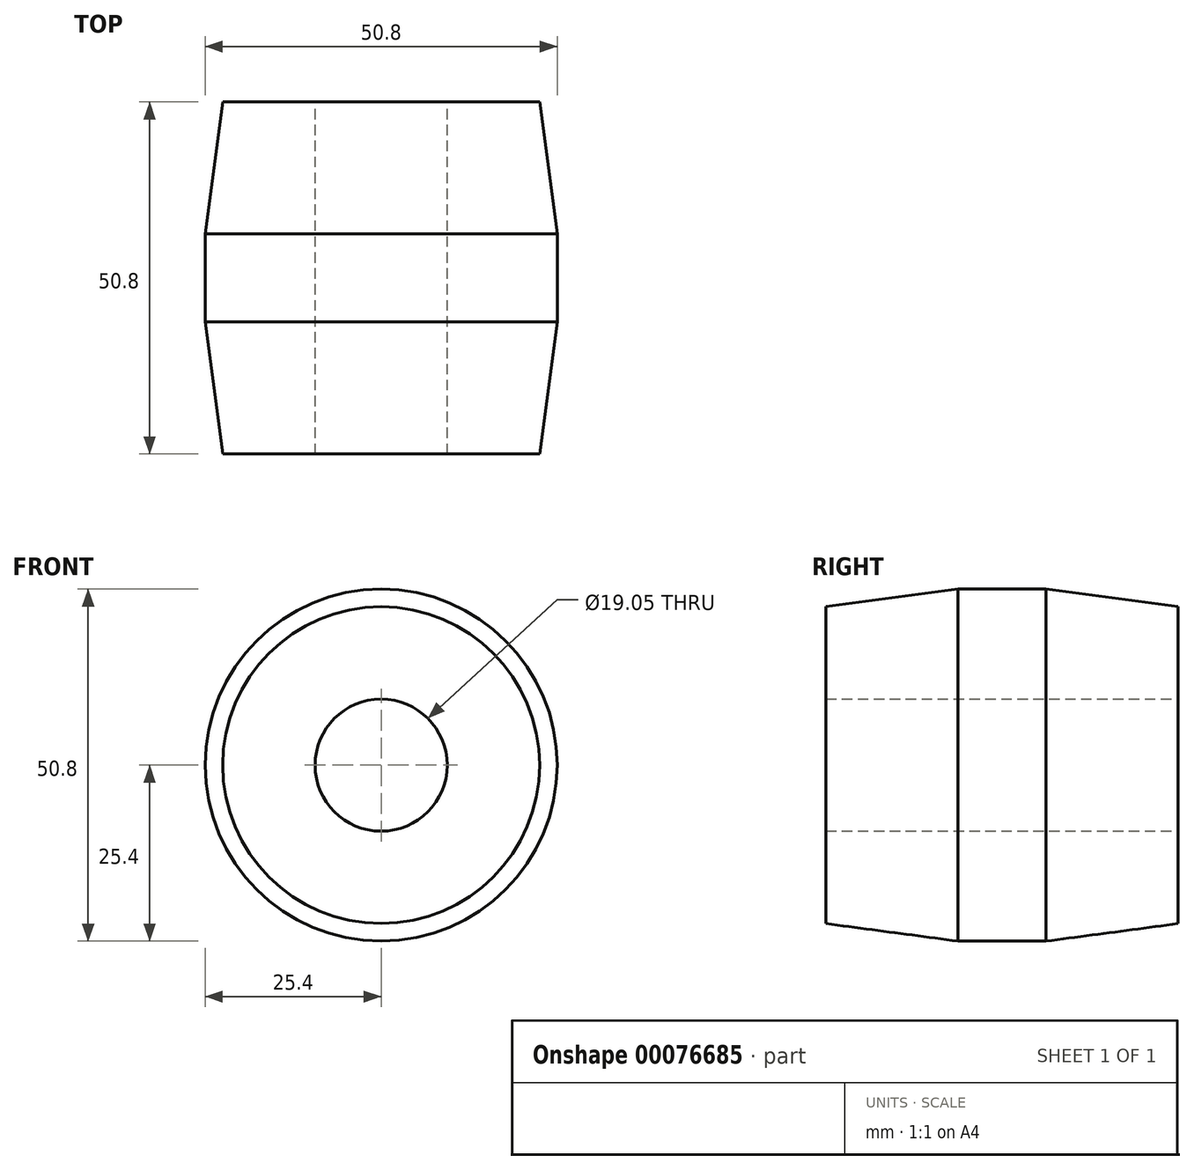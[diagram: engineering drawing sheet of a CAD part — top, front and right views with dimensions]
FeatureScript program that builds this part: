
annotation { "Feature Type Name" : "Feature", "Feature Type Description" : "" }
export const myFeature = defineFeature(function(context is Context, id is Id, definition is map)
    precondition{}
    {
        {
            var Q0;
            Q0=qCreatedBy(makeId("Front.planeOp"),FACE);
            var sketch = newSketch(context, id + "F0", { "sketchPlane" : qUnion([Q0])});
            skCircle(sketch, "E0", {"center": v(0, 0) * mm, "radius": 25.4 * mm});
            skCircle(sketch, "E1", {"center": v(0, 0) * mm, "radius": 9.53 * mm});
            skSolve(sketch);
        }
        {
            var Q0;
            Q0=makeQuery(id+"F0.imprint","IMPRINT",FACE,{"disambiguationData":[TD([[makeQuery(id+"F0.imprint","IMPRINT",EDGE,{"derivedFrom":sQuery(id+"F0.wireOp",EDGE,"E0")}),1.0]])]});
            extrude(context, id + "F1", {"entities" : qUnion([Q0]), "depth" : 50.8 * mm});
        }
        {
            var Q0;
            Q0=makeQuery(id+"F1.opExtrude","SWEPT_FACE",FACE,{"disambiguationData":[OSD([sQuery(id+"F0.wireOp",EDGE,"E0")])]});
            chamfer(context, id + "F2", {"entities" : qUnion([Q0]), "chamferType" : ChamferType.TWO_OFFSETS, "width1" : 19.05 * mm, "oppositeDirection" : false, "width2" : 2.54 * mm, "tangentPropagation" : true});
        }
    });
